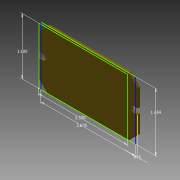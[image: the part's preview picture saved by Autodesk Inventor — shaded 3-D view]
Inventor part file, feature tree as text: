
AUTODESK INVENTOR PART (.ipt)
format: ipt  version: 2012 (Build 160160000, 160)  size: 109,568 bytes
history: native  units: in
note: dims shown in document units (in); Inventor stores cm internally (conversion verified against a paired STEP export)
features: sketch x3, extrude x2, chamfer x1
ambient origin geometry x8: Origin, YZ Plane, XZ Plane, XY Plane, X Axis, Y Axis, Z Axis, Center Point
bodies: Solid1 (feature_tree)
feature tree (6):
  extrude  "Extrusion1"  Depth=1.6535in
  chamfer  "Chamfer1"  Distance=0.0625in
  extrude  "Extrusion2"  Depth=0.1575in
  sketch  "Sketch3"  dims[d8=0.1575in d10=0.1969in d11=0.1969in d12=0.0625in d13=0.0in d14=2.6703in d15=0.0625in d16=2.5in d17=1.6535in d18=1.6in]
  sketch  "Sketch1"  dims[d0=2.7953in d1=1.6535in d2=0.0625in d3=0.0in]
  sketch  "Sketch2"  dims[d4=0.25in d5=0.125in d6=45.0deg d7=0.1575in]
